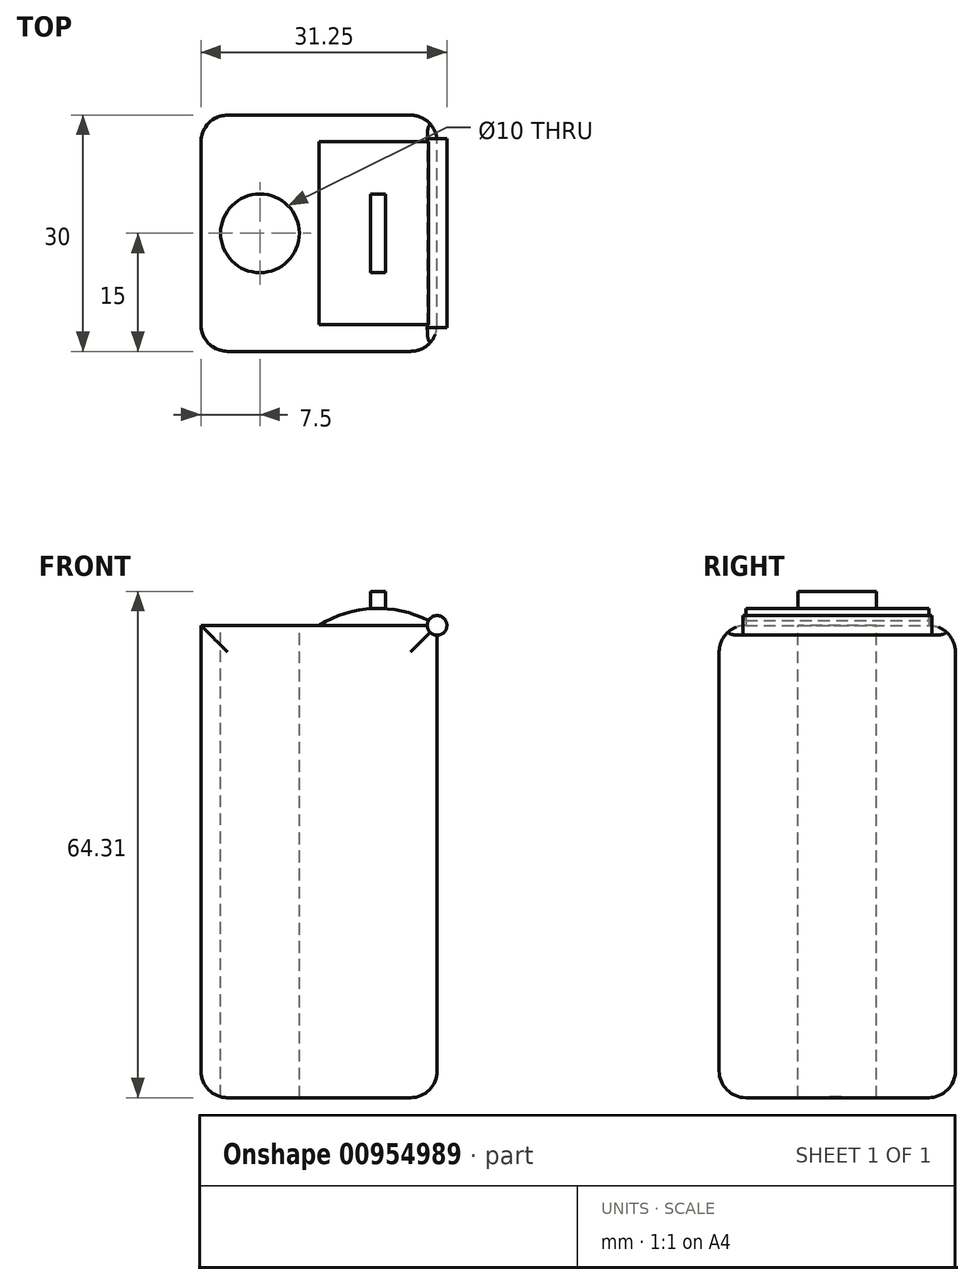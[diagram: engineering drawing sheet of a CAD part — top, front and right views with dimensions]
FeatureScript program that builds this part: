
annotation { "Feature Type Name" : "Feature", "Feature Type Description" : "" }
export const myFeature = defineFeature(function(context is Context, id is Id, definition is map)
    precondition{}
    {
        {
            var Q0;
            Q0=qCreatedBy(makeId("Front.planeOp"),FACE);
            var sketch = newSketch(context, id + "F0", { "sketchPlane" : qUnion([Q0])});
            skLineSegment(sketch, "E0.bottom", {"start": v(15, -30) * mm, "end": v(-15, -30) * mm});
            skLineSegment(sketch, "E0.top", {"start": v(15, 30) * mm, "end": v(-15, 30) * mm});
            skLineSegment(sketch, "E0.left", {"start": v(15, -30) * mm, "end": v(15, 30) * mm});
            skLineSegment(sketch, "E0.right", {"start": v(-15, -30) * mm, "end": v(-15, 30) * mm});
            skPoint(sketch, "E0.middle", {"position": v(0, 0) * mm});
            skCircle(sketch, "E1", {"center": v(15, 30) * mm, "radius": 1.25 * mm});
            skLineSegment(sketch, "E2.bottom", {"start": v(15, 30) * mm, "end": v(0, 30) * mm});
            skLineSegment(sketch, "E2.top", {"start": v(15, 32.15) * mm, "end": v(0, 32.15) * mm});
            skLineSegment(sketch, "E2.left", {"start": v(15, 30) * mm, "end": v(15, 32.15) * mm});
            skLineSegment(sketch, "E2.right", {"start": v(0, 30) * mm, "end": v(0, 32.15) * mm});
            skArc(sketch, "E3", {"start": v(15, 30) * mm, "mid": v(7.5, 32.15) * mm, "end": v(0, 30) * mm});
            skArc(sketch, "E4", {"start": v(-15, -30) * mm, "mid": v(0, -39.22) * mm, "end": v(15, -30) * mm});
            skLineSegment(sketch, "E5", {"start": v(0, -39.22) * mm, "end": v(0, -30) * mm});
            skLineSegment(sketch, "E6.bottom", {"start": v(8.46, 30) * mm, "end": v(6.54, 30) * mm});
            skLineSegment(sketch, "E6.top", {"start": v(8.46, 34.3) * mm, "end": v(6.54, 34.3) * mm});
            skLineSegment(sketch, "E6.left", {"start": v(8.46, 30) * mm, "end": v(8.46, 34.3) * mm});
            skLineSegment(sketch, "E6.right", {"start": v(6.54, 30) * mm, "end": v(6.54, 34.3) * mm});
            skPoint(sketch, "E6.middle", {"position": v(7.5, 32.15) * mm});
            skSolve(sketch);
        }
        {
            var Q0;
            {var subQ1=sQuery(id+"F0.wireOp",EDGE,"E6.top");Q0=makeQuery(id+"F0.imprint","IMPRINT",FACE,{"disambiguationData":[TD([[makeQuery(id+"F0.imprint","IMPRINT",EDGE,{"derivedFrom":subQ1}),1.0]])]});}
            var Q1;
            {var subQ3=sQuery(id+"F0.wireOp",EDGE,"E0.right");Q1=makeQuery(id+"F0.imprint","IMPRINT",FACE,{"disambiguationData":[TD([[makeQuery(id+"F0.imprint","IMPRINT",EDGE,{"derivedFrom":subQ3}),-1.0]])]});}
            extrude(context, id + "F1", {"entities" : qUnion([Q0, Q1]), "endBound" : BoundingType.SYMMETRIC, "depth" : 30 * mm, "offsetDistance" : 25 * mm});
        }
        {
            var Q0;
            {var subQ0=sQuery(id+"F0.wireOp",EDGE,"E1");var subQ1=sQuery(id+"F0.wireOp",EDGE,"E0.top");var subQ2=makeQuery(id+"F0.imprint","INTERSECT",VERTEX,{"derivedFrom":[subQ1,subQ0]});Q0=makeQuery(id+"F0.imprint","IMPRINT",FACE,{"disambiguationData":[TD([[makeQuery(id+"F0.imprint","IMPRINT",EDGE,{"disambiguationData":[TD([[subQ2,-1.0]])],"derivedFrom":subQ1}),-1.0]])]});}
            var Q1;
            {var subQ1=sQuery(id+"F0.wireOp",EDGE,"E0.top");var subQ6=sQuery(id+"F0.wireOp",EDGE,"E6.right");var subQ8=makeQuery(id+"F0.imprint","INTERSECT",VERTEX,{"derivedFrom":[subQ1,subQ6]});Q1=makeQuery(id+"F0.imprint","IMPRINT",FACE,{"disambiguationData":[TD([[makeQuery(id+"F0.imprint","IMPRINT",EDGE,{"disambiguationData":[TD([[subQ8,1.0]])],"derivedFrom":subQ1}),-1.0]])]});}
            var Q2;
            {var subQ1=sQuery(id+"F0.wireOp",EDGE,"E0.top");var subQ3=sQuery(id+"F0.wireOp",EDGE,"E6.right");var subQ4=makeQuery(id+"F0.imprint","INTERSECT",VERTEX,{"derivedFrom":[subQ1,subQ3]});Q2=makeQuery(id+"F0.imprint","IMPRINT",FACE,{"disambiguationData":[TD([[makeQuery(id+"F0.imprint","IMPRINT",EDGE,{"disambiguationData":[TD([[subQ4,-1.0]])],"derivedFrom":subQ3}),1.0]])]});}
            extrude(context, id + "F2", {"entities" : qUnion([Q0, Q1, Q2]), "endBound" : BoundingType.SYMMETRIC, "depth" : 23.24 * mm, "offsetDistance" : 25 * mm});
        }
        {
            var Q0;
            Q0=makeQuery(id+"F1.opExtrude","SWEPT_BODY",BODY,{"disambiguationData":[OSD([sQuery(id+"F0.wireOp",EDGE,"E2.top"),sQuery(id+"F0.wireOp",EDGE,"E6.top"),sQuery(id+"F0.wireOp",EDGE,"E6.left"),sQuery(id+"F0.wireOp",EDGE,"E6.right")])]});
            deleteBodies(context, id + "F3", {"entities" : qUnion([Q0])});
        }
        {
            var Q0;
            Q0=makeQuery(id+"F1.opExtrude","SWEPT_FACE",FACE,{"disambiguationData":[OSD([sQuery(id+"F0.wireOp",EDGE,"E0.bottom")])]});
            var Q1;
            Q1=makeQuery(id+"F1.opExtrude","CAP_FACE",FACE,{"disambiguationData":[OSD([sQuery(id+"F0.wireOp",EDGE,"E0.bottom"),sQuery(id+"F0.wireOp",EDGE,"E0.top"),sQuery(id+"F0.wireOp",EDGE,"E0.left"),sQuery(id+"F0.wireOp",EDGE,"E0.right"),sQuery(id+"F0.wireOp",EDGE,"E1")])],"isStart":true});
            var Q2;
            Q2=makeQuery(id+"F1.opExtrude","CAP_FACE",FACE,{"disambiguationData":[OSD([sQuery(id+"F0.wireOp",EDGE,"E0.bottom"),sQuery(id+"F0.wireOp",EDGE,"E0.top"),sQuery(id+"F0.wireOp",EDGE,"E0.left"),sQuery(id+"F0.wireOp",EDGE,"E0.right"),sQuery(id+"F0.wireOp",EDGE,"E1")])],"isStart":false});
            fillet(context, id + "F4", {"entities" : qUnion([Q0, Q1, Q2]), "radius" : 3.38 * mm, "tangentPropagation" : true, "allowEdgeOverflow" : false});
        }
        {
            var Q0;
            {var subQ0=sQuery(id+"F0.wireOp",EDGE,"E2.left");var subQ1=sQuery(id+"F0.wireOp",EDGE,"E1");var subQ2=makeQuery(id+"F0.imprint","INTERSECT",VERTEX,{"derivedFrom":[subQ1,subQ0]});Q0=makeQuery(id+"F0.imprint","IMPRINT",FACE,{"disambiguationData":[TD([[makeQuery(id+"F0.imprint","IMPRINT",EDGE,{"disambiguationData":[TD([[subQ2,-1.0]])],"derivedFrom":subQ1}),1.0]])]});}
            var Q1;
            {var subQ1=sQuery(id+"F0.wireOp",EDGE,"E0.left");var subQ3=sQuery(id+"F0.wireOp",EDGE,"E1");var subQ4=makeQuery(id+"F0.imprint","INTERSECT",VERTEX,{"derivedFrom":[subQ1,subQ3]});Q1=makeQuery(id+"F0.imprint","IMPRINT",FACE,{"disambiguationData":[TD([[makeQuery(id+"F0.imprint","IMPRINT",EDGE,{"disambiguationData":[TD([[subQ4,-1.0]])],"derivedFrom":subQ3}),1.0]])]});}
            var Q2;
            {var subQ0=sQuery(id+"F0.wireOp",EDGE,"E1");var subQ1=sQuery(id+"F0.wireOp",EDGE,"E0.top");var subQ2=makeQuery(id+"F0.imprint","INTERSECT",VERTEX,{"derivedFrom":[subQ1,subQ0]});Q2=makeQuery(id+"F0.imprint","IMPRINT",FACE,{"disambiguationData":[TD([[makeQuery(id+"F0.imprint","IMPRINT",EDGE,{"disambiguationData":[TD([[subQ2,-1.0]])],"derivedFrom":subQ0}),1.0]])]});}
            var Q3;
            {var subQ0=sQuery(id+"F0.wireOp",EDGE,"E1");var subQ1=sQuery(id+"F0.wireOp",EDGE,"E0.top");var subQ2=makeQuery(id+"F0.imprint","INTERSECT",VERTEX,{"derivedFrom":[subQ1,subQ0]});Q3=makeQuery(id+"F0.imprint","IMPRINT",FACE,{"disambiguationData":[TD([[makeQuery(id+"F0.imprint","IMPRINT",EDGE,{"disambiguationData":[TD([[subQ2,1.0]])],"derivedFrom":subQ0}),1.0]])]});}
            extrude(context, id + "F5", {"entities" : qUnion([Q0, Q1, Q2, Q3]), "endBound" : BoundingType.SYMMETRIC, "depth" : 24 * mm, "offsetDistance" : 25 * mm});
        }
        {
            var Q0;
            {var subQ1=sQuery(id+"F0.wireOp",EDGE,"E6.top");Q0=makeQuery(id+"F0.imprint","IMPRINT",FACE,{"disambiguationData":[TD([[makeQuery(id+"F0.imprint","IMPRINT",EDGE,{"derivedFrom":subQ1}),1.0]])]});}
            extrude(context, id + "F6", {"entities" : qUnion([Q0]), "endBound" : BoundingType.SYMMETRIC, "depth" : 10 * mm, "offsetDistance" : 25 * mm});
        }
        {
            var Q0;
            Q0=makeQuery(id+"F1.opExtrude","SWEPT_FACE",FACE,{"disambiguationData":[OSD([sQuery(id+"F0.wireOp",EDGE,"E0.top")])]});
            var sketch = newSketch(context, id + "F7", { "sketchPlane" : qUnion([Q0])});
            skLineSegment(sketch, "E7", {"start": v(-15, -11.62) * mm, "end": v(0, 11.62) * mm});
            skLineSegment(sketch, "E8", {"start": v(-15, 11.62) * mm, "end": v(0, -11.62) * mm});
            skCircle(sketch, "E9", {"center": v(-7.5, 0) * mm, "radius": 5 * mm});
            skSolve(sketch);
        }
        {
            var Q0;
            Q0=sQuery(id+"F7.wireOp",VERTEX,"E9.center");
            var Q1;
            Q1=makeQuery(id+"F1.opExtrude","SWEPT_BODY",BODY,{"disambiguationData":[OSD([sQuery(id+"F0.wireOp",EDGE,"E0.bottom"),sQuery(id+"F0.wireOp",EDGE,"E0.top"),sQuery(id+"F0.wireOp",EDGE,"E0.left"),sQuery(id+"F0.wireOp",EDGE,"E0.right"),sQuery(id+"F0.wireOp",EDGE,"E1")])]});
            hole(context, id + "F8", {"style" : HoleStyle.SIMPLE, "endStyle" : HoleEndStyle.THROUGH, "holeDiameter" : 10 * mm, "majorDiameter" : 5 * mm, "isTappedThrough" : true, "tappedDepth" : 12 * mm, "tapClearance" : 3, "locations" : qUnion([Q0]), "scope" : qUnion([Q1])});
        }
    });
